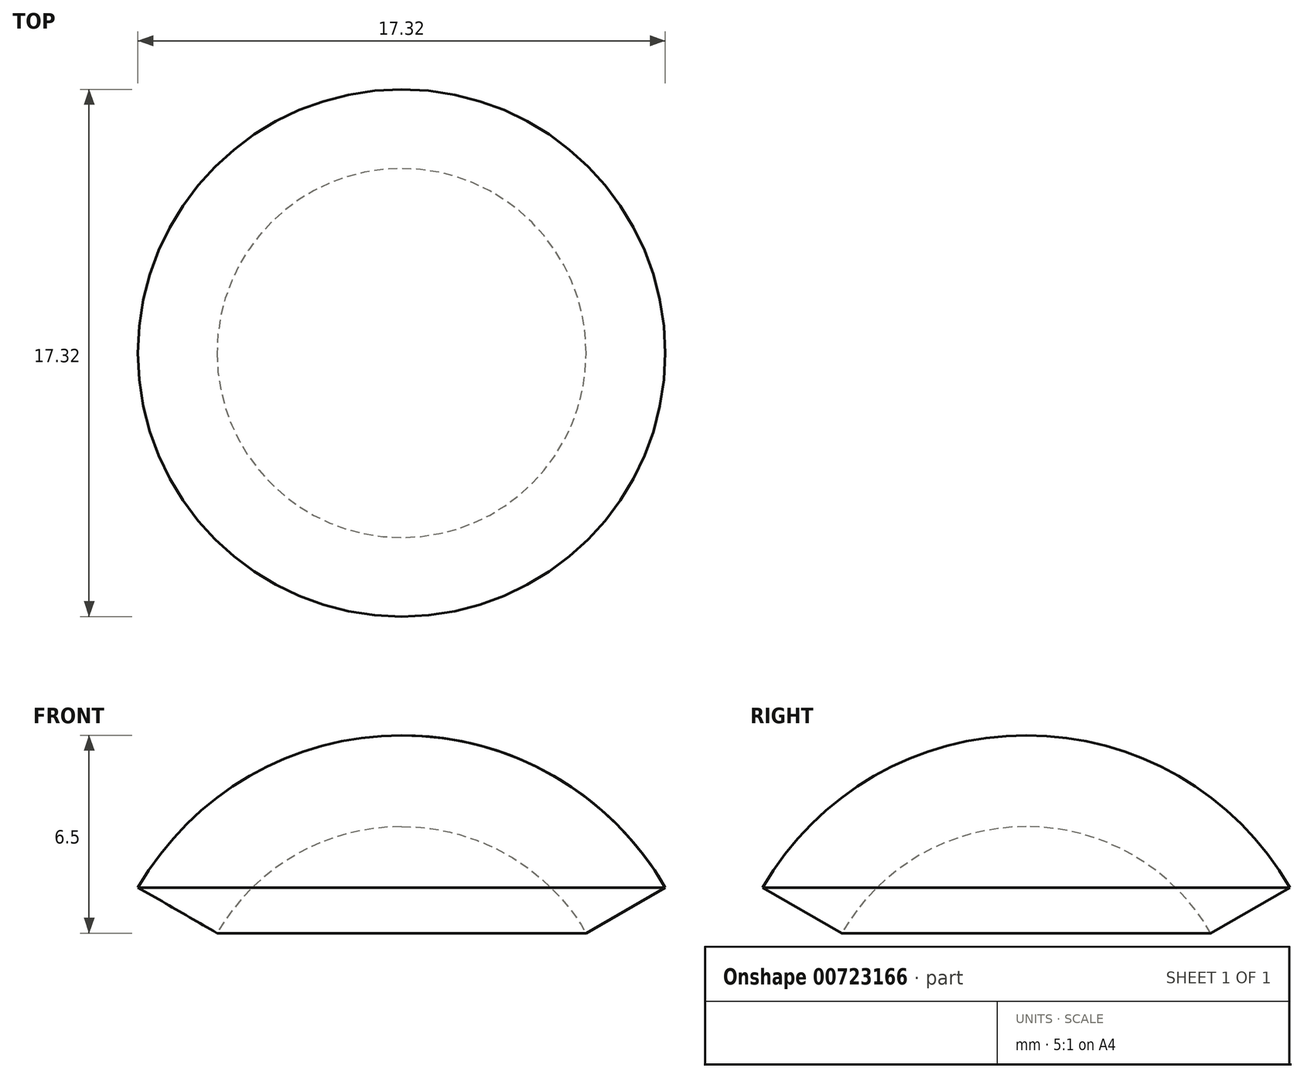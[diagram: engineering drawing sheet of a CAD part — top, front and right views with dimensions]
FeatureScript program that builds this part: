
annotation { "Feature Type Name" : "Feature", "Feature Type Description" : "" }
export const myFeature = defineFeature(function(context is Context, id is Id, definition is map)
    precondition{}
    {
        {
            var Q0;
            Q0=qCreatedBy(makeId("Front.planeOp"),FACE);
            var sketch = newSketch(context, id + "F0", { "sketchPlane" : qUnion([Q0])});
            skArc(sketch, "E0", {"start": v(6.06, 3.5) * mm, "mid": v(3.5, 6.06) * mm, "end": v(0, 7) * mm});
            skArc(sketch, "E1", {"start": v(8.66, 5) * mm, "mid": v(5, 8.66) * mm, "end": v(0, 10) * mm});
            skLineSegment(sketch, "E2", {"start": v(0, 10) * mm, "end": v(0, 7) * mm});
            skLineSegment(sketch, "E3", {"start": v(6.06, 3.5) * mm, "end": v(8.66, 5) * mm});
            skLineSegment(sketch, "E4", {"start": v(0, 0) * mm, "end": v(0, 123.55) * mm, "construction": true});
            skLineSegment(sketch, "E5", {"start": v(0, 0) * mm, "end": v(6.06, 3.5) * mm});
            skSolve(sketch);
        }
        {
            var Q0;
            Q0=qSketchRegion(id+"F0",true);
            var Q1;
            Q1=sQuery(id+"F0.wireOp",EDGE,"E4");
            revolve(context, id + "F1", {"surfaceOperationType" : NewSurfaceOperationType.NEW, "entities" : qUnion([Q0]), "axis" : qUnion([Q1]), "revolveType" : RevolveType.FULL});
        }
    });
